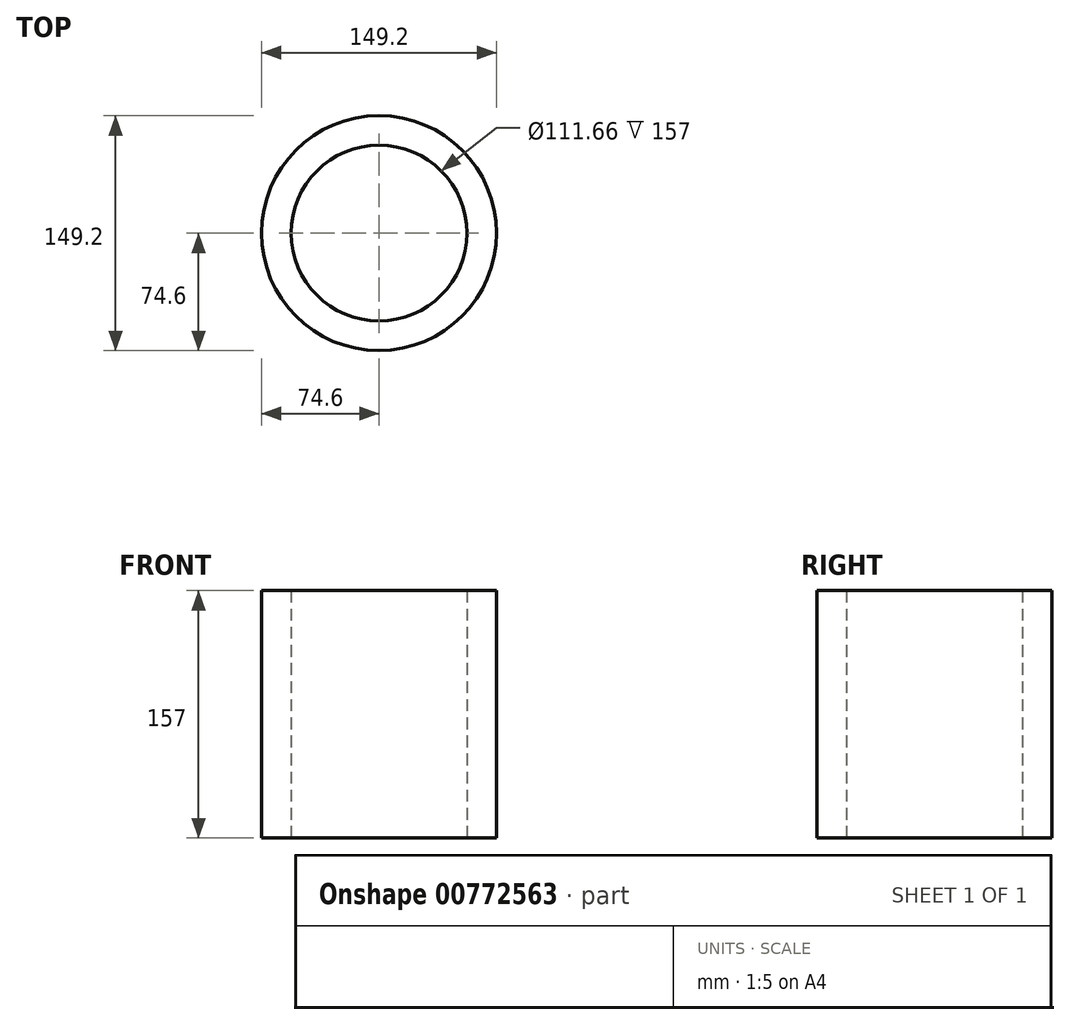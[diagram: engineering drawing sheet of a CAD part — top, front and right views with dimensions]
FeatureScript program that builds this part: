
annotation { "Feature Type Name" : "Feature", "Feature Type Description" : "" }
export const myFeature = defineFeature(function(context is Context, id is Id, definition is map)
    precondition{}
    {
        {
            var Q0;
            Q0=qCreatedBy(makeId("Top.planeOp"),FACE);
            var sketch = newSketch(context, id + "F0", { "sketchPlane" : qUnion([Q0])});
            skCircle(sketch, "E0", {"center": v(0, 0) * mm, "radius": 74.6 * mm});
            skCircle(sketch, "E1", {"center": v(0, 0) * mm, "radius": 55.83 * mm});
            skSolve(sketch);
        }
        {
            var Q0;
            Q0=makeQuery(id+"F0.imprint","IMPRINT",FACE,{"disambiguationData":[TD([[makeQuery(id+"F0.imprint","IMPRINT",EDGE,{"derivedFrom":sQuery(id+"F0.wireOp",EDGE,"E0")}),1.0]])]});
            extrude(context, id + "F1", {"entities" : qUnion([Q0]), "depth" : 157 * mm, "offsetDistance" : 25 * mm});
        }
    });
